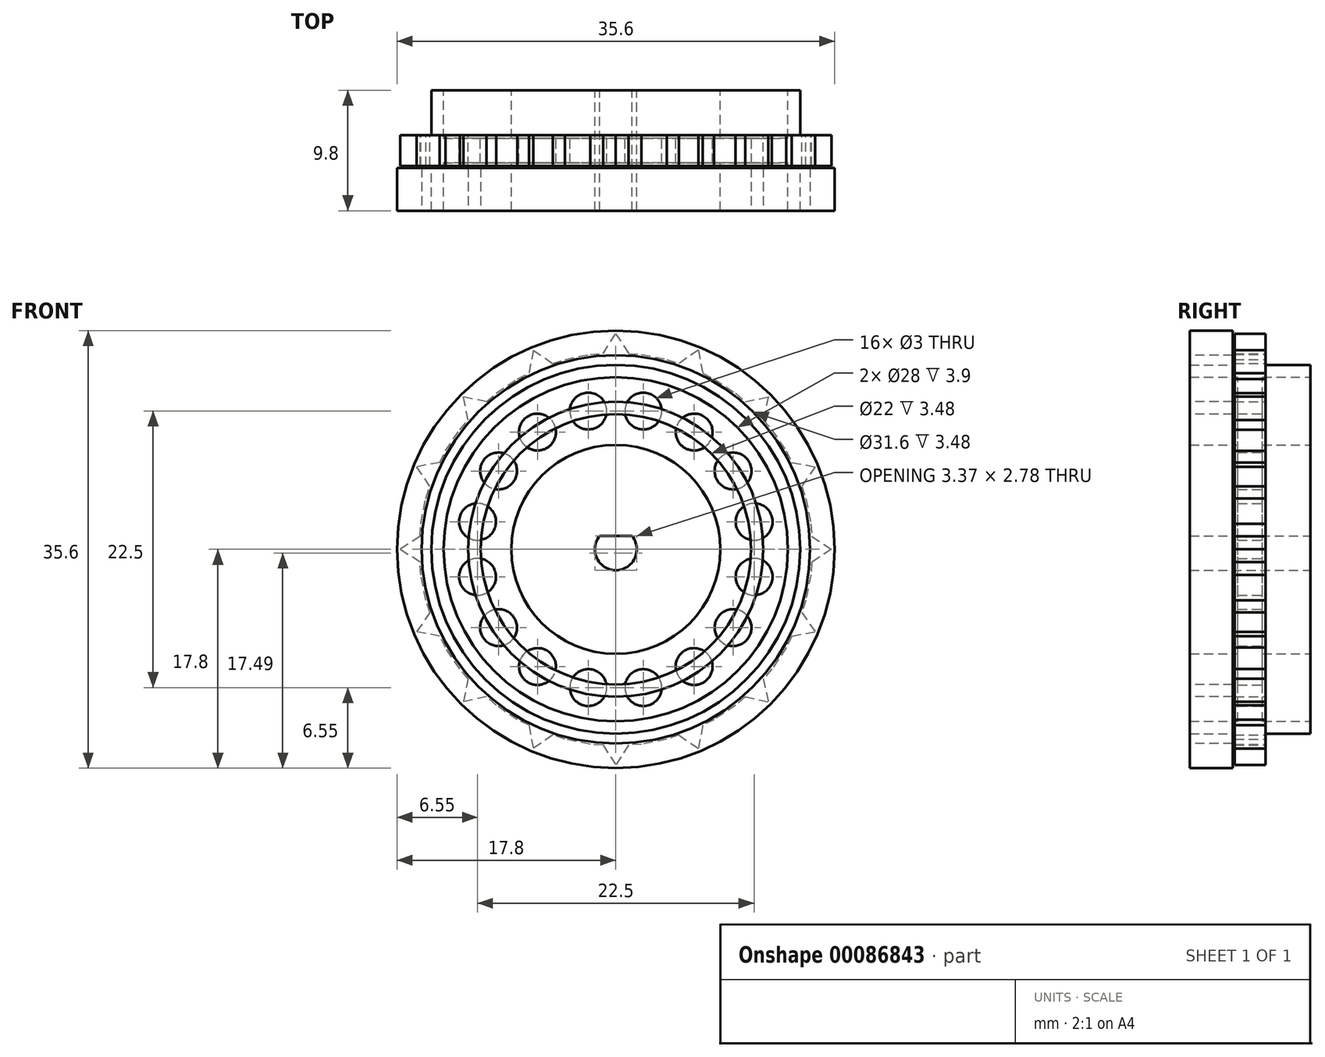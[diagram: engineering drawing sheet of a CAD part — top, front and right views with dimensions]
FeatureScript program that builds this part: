
annotation { "Feature Type Name" : "Feature", "Feature Type Description" : "" }
export const myFeature = defineFeature(function(context is Context, id is Id, definition is map)
    precondition{}
    {
        {
            var Q0;
            Q0=qCreatedBy(makeId("Front.planeOp"),FACE);
            var sketch = newSketch(context, id + "F0", { "sketchPlane" : qUnion([Q0])});
            skCircle(sketch, "E0", {"center": v(0, 0) * mm, "radius": 15 * mm});
            skCircle(sketch, "E1", {"center": v(0, 0) * mm, "radius": 14 * mm});
            skCircle(sketch, "E2", {"center": v(0, 0) * mm, "radius": 8.5 * mm});
            skLineSegment(sketch, "E3.1", {"start": v(2.09, 15.86) * mm, "end": v(4.14, 15.45) * mm});
            skLineSegment(sketch, "E3.4", {"start": v(8, 13.86) * mm, "end": v(9.74, 12.7) * mm});
            skLineSegment(sketch, "E3.7", {"start": v(12.7, 9.74) * mm, "end": v(13.86, 8) * mm});
            skLineSegment(sketch, "E3.10", {"start": v(15.45, 4.14) * mm, "end": v(15.86, 2.09) * mm});
            skLineSegment(sketch, "E3.13", {"start": v(15.86, -2.09) * mm, "end": v(15.45, -4.14) * mm});
            skLineSegment(sketch, "E3.16", {"start": v(13.86, -8) * mm, "end": v(12.7, -9.74) * mm});
            skLineSegment(sketch, "E3.19", {"start": v(9.74, -12.7) * mm, "end": v(8, -13.86) * mm});
            skLineSegment(sketch, "E3.22", {"start": v(4.14, -15.45) * mm, "end": v(2.09, -15.86) * mm});
            skLineSegment(sketch, "E3.25", {"start": v(-2.09, -15.86) * mm, "end": v(-4.14, -15.45) * mm});
            skLineSegment(sketch, "E3.28", {"start": v(-8, -13.86) * mm, "end": v(-9.74, -12.7) * mm});
            skLineSegment(sketch, "E3.31", {"start": v(-12.7, -9.74) * mm, "end": v(-13.86, -8) * mm});
            skLineSegment(sketch, "E3.34", {"start": v(-15.45, -4.14) * mm, "end": v(-15.86, -2.09) * mm});
            skLineSegment(sketch, "E3.37", {"start": v(-15.86, 2.09) * mm, "end": v(-15.45, 4.14) * mm});
            skLineSegment(sketch, "E3.40", {"start": v(-13.86, 8) * mm, "end": v(-12.7, 9.74) * mm});
            skLineSegment(sketch, "E3.43", {"start": v(-9.74, 12.7) * mm, "end": v(-8, 13.86) * mm});
            skLineSegment(sketch, "E3.46", {"start": v(-4.14, 15.45) * mm, "end": v(-2.09, 15.86) * mm});
            skLineSegment(sketch, "E4", {"start": v(-1.04, 15.93) * mm, "end": v(0, 17.55) * mm});
            skLineSegment(sketch, "E5", {"start": v(0, 17.55) * mm, "end": v(1.04, 15.93) * mm});
            skLineSegment(sketch, "E6", {"start": v(-6.72, 16.21) * mm, "end": v(-7.06, 14.32) * mm});
            skLineSegment(sketch, "E7", {"start": v(-6.72, 16.21) * mm, "end": v(-5.13, 15.12) * mm});
            skLineSegment(sketch, "E8", {"start": v(6.72, 16.21) * mm, "end": v(5.13, 15.12) * mm});
            skLineSegment(sketch, "E9", {"start": v(6.72, 16.21) * mm, "end": v(7.06, 14.32) * mm});
            skLineSegment(sketch, "E10", {"start": v(10.53, 12) * mm, "end": v(12.4, 12.4) * mm});
            skLineSegment(sketch, "E11", {"start": v(12.4, 12.4) * mm, "end": v(12, 10.53) * mm});
            skLineSegment(sketch, "E12", {"start": v(14.32, 7.06) * mm, "end": v(16.21, 6.72) * mm});
            skLineSegment(sketch, "E13", {"start": v(16.21, 6.72) * mm, "end": v(15.12, 5.13) * mm});
            skLineSegment(sketch, "E14", {"start": v(15.93, 1.04) * mm, "end": v(17.55, 0) * mm});
            skLineSegment(sketch, "E15", {"start": v(17.55, 0) * mm, "end": v(15.93, -1.04) * mm});
            skLineSegment(sketch, "E16", {"start": v(-10.53, 12) * mm, "end": v(-12.4, 12.4) * mm});
            skLineSegment(sketch, "E17", {"start": v(-12, 10.53) * mm, "end": v(-12.4, 12.4) * mm});
            skLineSegment(sketch, "E18", {"start": v(-14.32, 7.06) * mm, "end": v(-16.21, 6.72) * mm});
            skLineSegment(sketch, "E19", {"start": v(-15.12, 5.13) * mm, "end": v(-16.21, 6.72) * mm});
            skLineSegment(sketch, "E20", {"start": v(-15.93, 1.04) * mm, "end": v(-17.55, 0) * mm});
            skLineSegment(sketch, "E21", {"start": v(-15.93, -1.04) * mm, "end": v(-17.55, 0) * mm});
            skLineSegment(sketch, "E22", {"start": v(-15.12, -5.13) * mm, "end": v(-16.21, -6.72) * mm});
            skLineSegment(sketch, "E23", {"start": v(-14.32, -7.06) * mm, "end": v(-16.21, -6.72) * mm});
            skLineSegment(sketch, "E24", {"start": v(-12, -10.53) * mm, "end": v(-12.4, -12.4) * mm});
            skLineSegment(sketch, "E25", {"start": v(-10.53, -12) * mm, "end": v(-12.4, -12.4) * mm});
            skLineSegment(sketch, "E26", {"start": v(-7.06, -14.32) * mm, "end": v(-6.72, -16.21) * mm});
            skLineSegment(sketch, "E27", {"start": v(-5.13, -15.12) * mm, "end": v(-6.72, -16.21) * mm});
            skLineSegment(sketch, "E28", {"start": v(-1.04, -15.93) * mm, "end": v(0, -17.55) * mm});
            skLineSegment(sketch, "E29", {"start": v(1.04, -15.93) * mm, "end": v(0, -17.55) * mm});
            skLineSegment(sketch, "E30", {"start": v(5.13, -15.12) * mm, "end": v(6.72, -16.21) * mm});
            skLineSegment(sketch, "E31", {"start": v(7.06, -14.32) * mm, "end": v(6.72, -16.21) * mm});
            skLineSegment(sketch, "E32", {"start": v(10.53, -12) * mm, "end": v(12.4, -12.4) * mm});
            skLineSegment(sketch, "E33", {"start": v(12, -10.53) * mm, "end": v(12.4, -12.4) * mm});
            skLineSegment(sketch, "E34", {"start": v(14.32, -7.06) * mm, "end": v(16.21, -6.72) * mm});
            skLineSegment(sketch, "E35", {"start": v(15.12, -5.13) * mm, "end": v(16.21, -6.72) * mm});
            skLineSegment(sketch, "E36", {"start": v(0, 14) * mm, "end": v(0, 8.5) * mm, "construction": true});
            skCircle(sketch, "E37.cCircle", {"center": v(0, 0) * mm, "radius": 11.25 * mm, "construction": true});
            skLineSegment(sketch, "E37.0", {"start": v(-2.24, 11.25) * mm, "end": v(2.24, 11.25) * mm, "construction": true});
            skLineSegment(sketch, "E37.1", {"start": v(2.24, 11.25) * mm, "end": v(6.37, 9.54) * mm, "construction": true});
            skLineSegment(sketch, "E37.2", {"start": v(6.37, 9.54) * mm, "end": v(9.54, 6.37) * mm, "construction": true});
            skLineSegment(sketch, "E37.3", {"start": v(9.54, 6.37) * mm, "end": v(11.25, 2.24) * mm, "construction": true});
            skLineSegment(sketch, "E37.4", {"start": v(11.25, 2.24) * mm, "end": v(11.25, -2.24) * mm, "construction": true});
            skLineSegment(sketch, "E37.5", {"start": v(11.25, -2.24) * mm, "end": v(9.54, -6.37) * mm, "construction": true});
            skLineSegment(sketch, "E37.6", {"start": v(9.54, -6.37) * mm, "end": v(6.37, -9.54) * mm, "construction": true});
            skLineSegment(sketch, "E37.7", {"start": v(6.37, -9.54) * mm, "end": v(2.24, -11.25) * mm, "construction": true});
            skLineSegment(sketch, "E37.8", {"start": v(2.24, -11.25) * mm, "end": v(-2.24, -11.25) * mm, "construction": true});
            skLineSegment(sketch, "E37.9", {"start": v(-2.24, -11.25) * mm, "end": v(-6.37, -9.54) * mm, "construction": true});
            skLineSegment(sketch, "E37.10", {"start": v(-6.37, -9.54) * mm, "end": v(-9.54, -6.37) * mm, "construction": true});
            skLineSegment(sketch, "E37.11", {"start": v(-9.54, -6.37) * mm, "end": v(-11.25, -2.24) * mm, "construction": true});
            skLineSegment(sketch, "E37.12", {"start": v(-11.25, -2.24) * mm, "end": v(-11.25, 2.24) * mm, "construction": true});
            skLineSegment(sketch, "E37.13", {"start": v(-11.25, 2.24) * mm, "end": v(-9.54, 6.37) * mm, "construction": true});
            skLineSegment(sketch, "E37.14", {"start": v(-9.54, 6.37) * mm, "end": v(-6.37, 9.54) * mm, "construction": true});
            skLineSegment(sketch, "E37.15", {"start": v(-6.37, 9.54) * mm, "end": v(-2.24, 11.25) * mm, "construction": true});
            skPoint(sketch, "E37.0.midPoint", {"position": v(0, 11.25) * mm});
            skCircle(sketch, "E38", {"center": v(-6.37, 9.54) * mm, "radius": 1.5 * mm});
            skCircle(sketch, "E39", {"center": v(-2.24, 11.25) * mm, "radius": 1.5 * mm});
            skCircle(sketch, "E40", {"center": v(2.24, 11.25) * mm, "radius": 1.5 * mm});
            skCircle(sketch, "E41", {"center": v(6.37, 9.54) * mm, "radius": 1.5 * mm});
            skCircle(sketch, "E42", {"center": v(9.54, 6.37) * mm, "radius": 1.5 * mm});
            skCircle(sketch, "E43", {"center": v(11.25, 2.24) * mm, "radius": 1.5 * mm});
            skCircle(sketch, "E44", {"center": v(11.25, -2.24) * mm, "radius": 1.5 * mm});
            skCircle(sketch, "E45", {"center": v(9.54, -6.37) * mm, "radius": 1.5 * mm});
            skCircle(sketch, "E46", {"center": v(6.37, -9.54) * mm, "radius": 1.5 * mm});
            skCircle(sketch, "E47", {"center": v(2.24, -11.25) * mm, "radius": 1.5 * mm});
            skCircle(sketch, "E48", {"center": v(-2.24, -11.25) * mm, "radius": 1.5 * mm});
            skCircle(sketch, "E49", {"center": v(-6.37, -9.54) * mm, "radius": 1.5 * mm});
            skCircle(sketch, "E50", {"center": v(-9.54, -6.37) * mm, "radius": 1.5 * mm});
            skCircle(sketch, "E51", {"center": v(-11.25, -2.24) * mm, "radius": 1.5 * mm});
            skCircle(sketch, "E52", {"center": v(-11.25, 2.24) * mm, "radius": 1.5 * mm});
            skCircle(sketch, "E53", {"center": v(-9.54, 6.37) * mm, "radius": 1.5 * mm});
            skLineSegment(sketch, "E54", {"start": v(-15.45, 4.14) * mm, "end": v(-15.12, 5.13) * mm});
            skLineSegment(sketch, "E55", {"start": v(-14.32, 7.06) * mm, "end": v(-13.86, 8) * mm});
            skLineSegment(sketch, "E56", {"start": v(-12.7, 9.74) * mm, "end": v(-12, 10.53) * mm});
            skLineSegment(sketch, "E57", {"start": v(-10.53, 12) * mm, "end": v(-9.74, 12.7) * mm});
            skLineSegment(sketch, "E58", {"start": v(-8, 13.86) * mm, "end": v(-7.06, 14.32) * mm});
            skLineSegment(sketch, "E59", {"start": v(-5.13, 15.12) * mm, "end": v(-4.14, 15.45) * mm});
            skLineSegment(sketch, "E60", {"start": v(-2.09, 15.86) * mm, "end": v(-1.04, 15.93) * mm});
            skLineSegment(sketch, "E61", {"start": v(1.04, 15.93) * mm, "end": v(2.09, 15.86) * mm});
            skLineSegment(sketch, "E62", {"start": v(4.14, 15.45) * mm, "end": v(5.13, 15.12) * mm});
            skLineSegment(sketch, "E63", {"start": v(7.06, 14.32) * mm, "end": v(8, 13.86) * mm});
            skLineSegment(sketch, "E64", {"start": v(9.74, 12.7) * mm, "end": v(10.53, 12) * mm});
            skLineSegment(sketch, "E65", {"start": v(12, 10.53) * mm, "end": v(12.7, 9.74) * mm});
            skLineSegment(sketch, "E66", {"start": v(13.86, 8) * mm, "end": v(14.32, 7.06) * mm});
            skLineSegment(sketch, "E67", {"start": v(15.12, 5.13) * mm, "end": v(15.45, 4.14) * mm});
            skLineSegment(sketch, "E68", {"start": v(15.86, 2.09) * mm, "end": v(15.93, 1.04) * mm});
            skLineSegment(sketch, "E69", {"start": v(15.93, -1.04) * mm, "end": v(15.86, -2.09) * mm});
            skLineSegment(sketch, "E70", {"start": v(15.45, -4.14) * mm, "end": v(15.12, -5.13) * mm});
            skLineSegment(sketch, "E71", {"start": v(14.32, -7.06) * mm, "end": v(13.86, -8) * mm});
            skLineSegment(sketch, "E72", {"start": v(12.7, -9.74) * mm, "end": v(12, -10.53) * mm});
            skLineSegment(sketch, "E73", {"start": v(10.53, -12) * mm, "end": v(9.74, -12.7) * mm});
            skLineSegment(sketch, "E74", {"start": v(8, -13.86) * mm, "end": v(7.06, -14.32) * mm});
            skLineSegment(sketch, "E75", {"start": v(5.13, -15.12) * mm, "end": v(4.14, -15.45) * mm});
            skLineSegment(sketch, "E76", {"start": v(2.09, -15.86) * mm, "end": v(1.04, -15.93) * mm});
            skLineSegment(sketch, "E77", {"start": v(-1.04, -15.93) * mm, "end": v(-2.09, -15.86) * mm});
            skLineSegment(sketch, "E78", {"start": v(-4.14, -15.45) * mm, "end": v(-5.13, -15.12) * mm});
            skLineSegment(sketch, "E79", {"start": v(-7.06, -14.32) * mm, "end": v(-8, -13.86) * mm});
            skLineSegment(sketch, "E80", {"start": v(-9.74, -12.7) * mm, "end": v(-10.53, -12) * mm});
            skLineSegment(sketch, "E81", {"start": v(-12, -10.53) * mm, "end": v(-12.7, -9.74) * mm});
            skLineSegment(sketch, "E82", {"start": v(-13.86, -8) * mm, "end": v(-14.32, -7.06) * mm});
            skLineSegment(sketch, "E83", {"start": v(-15.12, -5.13) * mm, "end": v(-15.45, -4.14) * mm});
            skLineSegment(sketch, "E84", {"start": v(-15.86, -2.09) * mm, "end": v(-15.93, -1.04) * mm});
            skLineSegment(sketch, "E85", {"start": v(-15.93, 1.04) * mm, "end": v(-15.86, 2.09) * mm});
            skLineSegment(sketch, "E86", {"start": v(-1.31, 1.08) * mm, "end": v(1.31, 1.08) * mm});
            skArc(sketch, "E87", {"start": v(-1.31, 1.08) * mm, "mid": v(0, -1.7) * mm, "end": v(1.31, 1.08) * mm});
            skSolve(sketch);
        }
        {
            var Q0;
            Q0=makeQuery(id+"F0.imprint","IMPRINT",FACE,{"disambiguationData":[TD([[makeQuery(id+"F0.imprint","IMPRINT",EDGE,{"derivedFrom":sQuery(id+"F0.wireOp",EDGE,"E0")}),-1.0]])]});
            extrude(context, id + "F1", {"entities" : qUnion([Q0]), "depth" : 2.5 * mm, "symmetric" : true});
        }
        {
            var Q0;
            Q0=makeQuery(id+"F0.imprint","IMPRINT",FACE,{"disambiguationData":[TD([[makeQuery(id+"F0.imprint","IMPRINT",EDGE,{"derivedFrom":sQuery(id+"F0.wireOp",EDGE,"E0")}),1.0]])]});
            extrude(context, id + "F2", {"entities" : qUnion([Q0]), "operationType" : NewBodyOperationType.ADD, "depth" : 9.8 * mm, "symmetric" : true});
        }
        {
            var Q0;
            Q0=makeQuery(id+"F0.imprint","IMPRINT",FACE,{"disambiguationData":[TD([[makeQuery(id+"F0.imprint","IMPRINT",EDGE,{"derivedFrom":sQuery(id+"F0.wireOp",EDGE,"E1")}),1.0]])]});
            extrude(context, id + "F3", {"entities" : qUnion([Q0]), "operationType" : NewBodyOperationType.ADD, "depth" : 2 * mm, "symmetric" : true});
        }
        {
            var Q0;
            Q0=makeQuery(id+"F0.imprint","IMPRINT",FACE,{"disambiguationData":[TD([[makeQuery(id+"F0.imprint","IMPRINT",EDGE,{"derivedFrom":sQuery(id+"F0.wireOp",EDGE,"E2")}),1.0]])]});
            extrude(context, id + "F4", {"entities" : qUnion([Q0]), "operationType" : NewBodyOperationType.ADD, "depth" : 9.8 * mm, "symmetric" : true});
        }
        {
            var Q0;
            Q0=makeQuery(id+"F2.opExtrude","CAP_FACE",FACE,{"disambiguationData":[OSD([sQuery(id+"F0.wireOp",EDGE,"E0"),sQuery(id+"F0.wireOp",EDGE,"E1")])],"isStart":false});
            var sketch = newSketch(context, id + "F5", { "sketchPlane" : qUnion([Q0])});
            skCircle(sketch, "E88", {"center": v(0, 0) * mm, "radius": 15.8 * mm});
            skCircle(sketch, "E89", {"center": v(0, 0) * mm, "radius": 17.8 * mm});
            skCircle(sketch, "E90", {"center": v(0, 0) * mm, "radius": 11 * mm});
            skCircle(sketch, "E91", {"center": v(0, 0) * mm, "radius": 12 * mm});
            skSolve(sketch);
        }
        {
            var Q0;
            Q0=makeQuery(id+"F5.imprint","IMPRINT",FACE,{"disambiguationData":[TD([[makeQuery(id+"F5.imprint","IMPRINT",EDGE,{"derivedFrom":sQuery(id+"F5.wireOp",EDGE,"E88")}),-1.0]])]});
            var Q1;
            Q1=makeQuery(id+"F5.imprint","IMPRINT",FACE,{"disambiguationData":[TD([[makeQuery(id+"F5.imprint","IMPRINT",EDGE,{"derivedFrom":sQuery(id+"F5.wireOp",EDGE,"E90")}),-1.0]])]});
            extrude(context, id + "F6", {"entities" : qUnion([Q0, Q1]), "oppositeDirection" : true, "depth" : 3.48 * mm});
        }
    });
